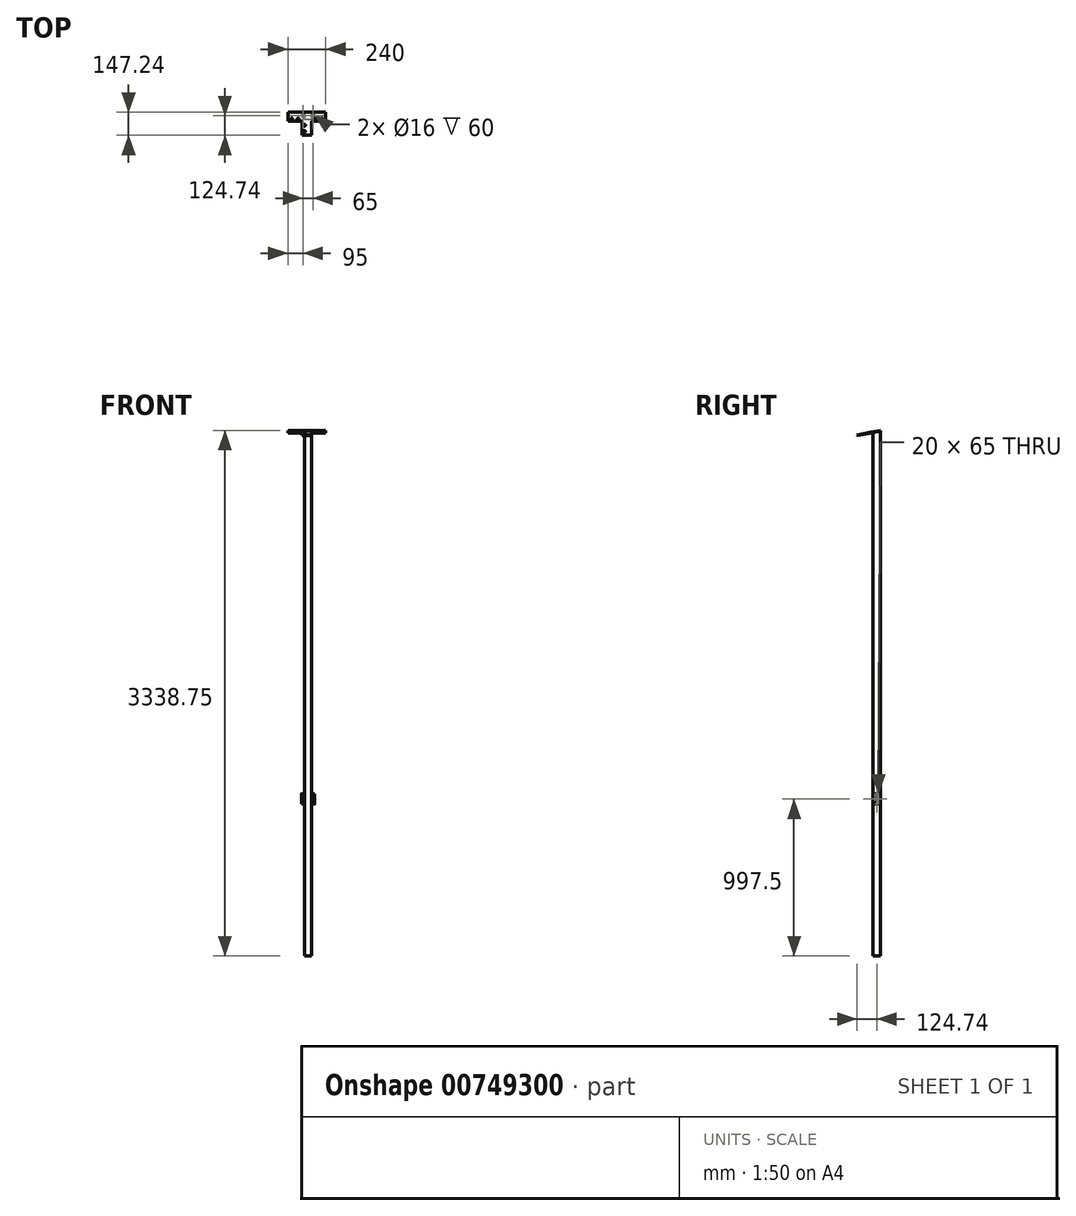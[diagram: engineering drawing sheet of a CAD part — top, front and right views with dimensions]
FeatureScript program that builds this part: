
annotation { "Feature Type Name" : "Feature", "Feature Type Description" : "" }
export const myFeature = defineFeature(function(context is Context, id is Id, definition is map)
    precondition{}
    {
        {
            var Q0;
            Q0=qCreatedBy(makeId("Top.planeOp"),FACE);
            var sketch = newSketch(context, id + "F0", { "sketchPlane" : qUnion([Q0])});
            skLineSegment(sketch, "E0.bottom", {"start": v(22.5, -22.5) * mm, "end": v(-22.5, -22.5) * mm});
            skLineSegment(sketch, "E0.top", {"start": v(22.5, 22.5) * mm, "end": v(-22.5, 22.5) * mm});
            skLineSegment(sketch, "E0.left", {"start": v(22.5, -22.5) * mm, "end": v(22.5, 22.5) * mm});
            skLineSegment(sketch, "E0.right", {"start": v(-22.5, -22.5) * mm, "end": v(-22.5, 22.5) * mm});
            skPoint(sketch, "E0.middle", {"position": v(0, 0) * mm});
            skSolve(sketch);
        }
        {
            var Q0;
            Q0=qSketchRegion(id+"F0",true);
            extrude(context, id + "F1", {"entities" : qUnion([Q0]), "depth" : 3330 * mm, "offsetDistance" : 25 * mm});
        }
        {
            var Q0;
            Q0=qCreatedBy(makeId("Top.planeOp"),FACE);
            cPlane(context, id + "F2", {"entities" : qUnion([Q0]), "cplaneType" : CPlaneType.OFFSET, "offset" : 965 * mm, "width" : 150 * mm, "height" : 150 * mm});
        }
        {
            var Q0;
            Q0=qCreatedBy(id+"F2.planeOp",FACE);
            var sketch = newSketch(context, id + "F3", { "sketchPlane" : qUnion([Q0])});
            skLineSegment(sketch, "E1", {"start": v(0, 0) * mm, "end": v(22.5, 0) * mm});
            skLineSegment(sketch, "E2", {"start": v(22.5, 0) * mm, "end": v(32.5, 0) * mm});
            skCircle(sketch, "E3", {"center": v(32.5, 0) * mm, "radius": 10 * mm});
            skLineSegment(sketch, "E4", {"start": v(32.5, 0) * mm, "end": v(32.5, 2) * mm});
            skLineSegment(sketch, "E5", {"start": v(32.5, 0) * mm, "end": v(32.5, -2) * mm});
            skLineSegment(sketch, "E6", {"start": v(32.5, -2) * mm, "end": v(22.5, -2) * mm});
            skLineSegment(sketch, "E7", {"start": v(32.5, 2) * mm, "end": v(22.5, 2) * mm});
            skLineSegment(sketch, "E8", {"start": v(0, 0) * mm, "end": v(-22.5, 0) * mm});
            skLineSegment(sketch, "E9", {"start": v(-22.5, 0) * mm, "end": v(-32.5, 0) * mm});
            skCircle(sketch, "E10", {"center": v(-32.5, 0) * mm, "radius": 10 * mm});
            skLineSegment(sketch, "E11", {"start": v(32.5, 2) * mm, "end": v(32.5, 10) * mm});
            skLineSegment(sketch, "E12", {"start": v(32.5, 10) * mm, "end": v(22.5, 10) * mm});
            skLineSegment(sketch, "E13", {"start": v(32.5, -2) * mm, "end": v(32.5, -10) * mm});
            skLineSegment(sketch, "E14", {"start": v(32.5, -10) * mm, "end": v(22.5, -10) * mm});
            skLineSegment(sketch, "E15", {"start": v(22.5, -10) * mm, "end": v(22.5, 10) * mm});
            skLineSegment(sketch, "E16", {"start": v(-32.5, 10) * mm, "end": v(-22.48, 10) * mm});
            skLineSegment(sketch, "E17", {"start": v(-22.48, 10) * mm, "end": v(-22.48, -10) * mm});
            skLineSegment(sketch, "E18", {"start": v(-22.48, -10) * mm, "end": v(-32.5, -10) * mm});
            skSolve(sketch);
        }
        {
            var Q0;
            Q0=qSketchRegion(id+"F3",true);
            extrude(context, id + "F4", {"entities" : qUnion([Q0]), "operationType" : NewBodyOperationType.ADD, "depth" : 5 * mm, "offsetDistance" : 25 * mm});
        }
        {
            var Q0;
            Q0=makeQuery(id+"F4.opExtrude","CAP_FACE",FACE,{"disambiguationData":[OSD([sQuery(id+"F3.wireOp",EDGE,"E3")])],"isStart":false});
            var sketch = newSketch(context, id + "F5", { "sketchPlane" : qUnion([Q0])});
            skCircle(sketch, "E19", {"center": v(32.5, 0) * mm, "radius": 10 * mm});
            skCircle(sketch, "E20", {"center": v(32.5, 0) * mm, "radius": 8 * mm});
            skCircle(sketch, "E21", {"center": v(-32.5, 0) * mm, "radius": 8 * mm});
            skCircle(sketch, "E22", {"center": v(-32.5, 0) * mm, "radius": 10 * mm});
            skLineSegment(sketch, "E23.0", {"start": v(32.5, -10) * mm, "end": v(22.5, -10) * mm});
            skLineSegment(sketch, "E24.0", {"start": v(22.5, -10) * mm, "end": v(22.5, 10) * mm});
            skPoint(sketch, "E25.0", {"position": v(27.5, 10) * mm});
            skLineSegment(sketch, "E26.0", {"start": v(32.5, 10) * mm, "end": v(22.5, 10) * mm});
            skLineSegment(sketch, "E27.0", {"start": v(-32.5, 10) * mm, "end": v(-22.5, 10) * mm});
            skLineSegment(sketch, "E28.0", {"start": v(-22.5, -10) * mm, "end": v(-22.5, 10) * mm});
            skLineSegment(sketch, "E29.0", {"start": v(-22.5, -10) * mm, "end": v(-32.5, -10) * mm});
            skSolve(sketch);
        }
        {
            var Q0;
            Q0=makeQuery(id+"F5.imprint","IMPRINT",FACE,{"disambiguationData":[TD([[makeQuery(id+"F5.imprint","IMPRINT",EDGE,{"derivedFrom":sQuery(id+"F5.wireOp",EDGE,"E19")}),1.0]])]});
            var Q1;
            Q1=makeQuery(id+"F5.imprint","IMPRINT",FACE,{"disambiguationData":[TD([[makeQuery(id+"F5.imprint","IMPRINT",EDGE,{"derivedFrom":sQuery(id+"F5.wireOp",EDGE,"E21")}),-1.0]])]});
            var Q2;
            {var subQ0=sQuery(id+"F5.wireOp",EDGE,"E29.0");Q2=makeQuery(id+"F5.imprint","IMPRINT",FACE,{"disambiguationData":[TD([[makeQuery(id+"F5.imprint","IMPRINT",EDGE,{"derivedFrom":subQ0}),-1.0]])]});}
            var Q3;
            {var subQ0=sQuery(id+"F5.wireOp",EDGE,"E27.0");Q3=makeQuery(id+"F5.imprint","IMPRINT",FACE,{"disambiguationData":[TD([[makeQuery(id+"F5.imprint","IMPRINT",EDGE,{"derivedFrom":subQ0}),-1.0]])]});}
            var Q4;
            {var subQ0=sQuery(id+"F5.wireOp",EDGE,"E26.0");Q4=makeQuery(id+"F5.imprint","IMPRINT",FACE,{"disambiguationData":[TD([[makeQuery(id+"F5.imprint","IMPRINT",EDGE,{"derivedFrom":subQ0}),1.0]])]});}
            var Q5;
            {var subQ0=sQuery(id+"F5.wireOp",EDGE,"E23.0");Q5=makeQuery(id+"F5.imprint","IMPRINT",FACE,{"disambiguationData":[TD([[makeQuery(id+"F5.imprint","IMPRINT",EDGE,{"derivedFrom":subQ0}),-1.0]])]});}
            extrude(context, id + "F6", {"entities" : qUnion([Q0, Q1, Q2, Q3, Q4, Q5]), "operationType" : NewBodyOperationType.ADD, "depth" : 60 * mm, "offsetDistance" : 25 * mm});
        }
        {
            var Q0;
            Q0=makeQuery(id+"F1.opExtrude","CAP_EDGE",EDGE,{"disambiguationData":[OSD([sQuery(id+"F0.wireOp",EDGE,"E0.bottom")])],"isStart":false});
            cPlane(context, id + "F7", {"entities" : qUnion([Q0]), "cplaneType" : CPlaneType.LINE_ANGLE, "offset" : 25 * mm, "angle" : 101 * degree, "oppositeDirection" : true, "width" : 150 * mm, "height" : 150 * mm});
        }
        {
            var Q0;
            Q0=makeQuery(id+"F1.opExtrude","CAP_FACE",FACE,{"disambiguationData":[OSD([sQuery(id+"F0.wireOp",EDGE,"E0.bottom"),sQuery(id+"F0.wireOp",EDGE,"E0.top"),sQuery(id+"F0.wireOp",EDGE,"E0.left"),sQuery(id+"F0.wireOp",EDGE,"E0.right")])],"isStart":false});
            var sketch = newSketch(context, id + "F8", { "sketchPlane" : qUnion([Q0])});
            skLineSegment(sketch, "E30.bottom", {"start": v(-22.5, 22.5) * mm, "end": v(22.5, 22.5) * mm});
            skLineSegment(sketch, "E30.top", {"start": v(-22.5, -22.5) * mm, "end": v(22.5, -22.5) * mm});
            skLineSegment(sketch, "E30.left", {"start": v(-22.5, 22.5) * mm, "end": v(-22.5, -22.5) * mm});
            skLineSegment(sketch, "E30.right", {"start": v(22.5, 22.5) * mm, "end": v(22.5, -22.5) * mm});
            skSolve(sketch);
        }
        {
            var Q0;
            Q0=qCreatedBy(id+"F7.planeOp",FACE);
            var sketch = newSketch(context, id + "F9", { "sketchPlane" : qUnion([Q0])});
            skLineSegment(sketch, "E31.bottom", {"start": v(-22.5, -659.15) * mm, "end": v(22.5, -659.15) * mm});
            skLineSegment(sketch, "E31.top", {"start": v(-22.5, -613.3) * mm, "end": v(22.5, -613.3) * mm});
            skLineSegment(sketch, "E31.left", {"start": v(-22.5, -659.15) * mm, "end": v(-22.5, -613.3) * mm});
            skLineSegment(sketch, "E31.right", {"start": v(22.5, -659.15) * mm, "end": v(22.5, -613.3) * mm});
            skSolve(sketch);
        }
        {
            var Q0;
            Q0=makeQuery(id+"F9.imprint","IMPRINT",FACE,{"disambiguationData":[TD([[makeQuery(id+"F9.imprint","IMPRINT",EDGE,{"derivedFrom":sQuery(id+"F9.wireOp",EDGE,"E31.bottom")}),1.0]])]});
            extrude(context, id + "F10", {"entities" : qUnion([Q0]), "operationType" : NewBodyOperationType.ADD, "depth" : 25 * mm, "offsetDistance" : 25 * mm});
        }
        {
            var Q0;
            Q0=qCreatedBy(id+"F7.planeOp",FACE);
            var sketch = newSketch(context, id + "F11", { "sketchPlane" : qUnion([Q0])});
            skLineSegment(sketch, "E32.bottom", {"start": v(-37.5, -659.15) * mm, "end": v(22.5, -659.15) * mm});
            skLineSegment(sketch, "E32.top", {"start": v(-37.5, -599.15) * mm, "end": v(22.5, -599.15) * mm});
            skLineSegment(sketch, "E32.left", {"start": v(-37.5, -659.15) * mm, "end": v(-37.5, -599.15) * mm});
            skLineSegment(sketch, "E32.right", {"start": v(22.5, -659.15) * mm, "end": v(22.5, -599.15) * mm});
            skLineSegment(sketch, "E33.bottom", {"start": v(22.5, -659.15) * mm, "end": v(112.5, -659.15) * mm});
            skLineSegment(sketch, "E33.top", {"start": v(22.5, -599.15) * mm, "end": v(112.5, -599.15) * mm});
            skLineSegment(sketch, "E33.right", {"start": v(112.5, -659.15) * mm, "end": v(112.5, -599.15) * mm});
            skLineSegment(sketch, "E34.top", {"start": v(-37.5, -509.15) * mm, "end": v(22.5, -509.15) * mm});
            skLineSegment(sketch, "E34.left", {"start": v(-37.5, -599.15) * mm, "end": v(-37.5, -509.15) * mm});
            skLineSegment(sketch, "E34.right", {"start": v(22.5, -599.15) * mm, "end": v(22.5, -509.15) * mm});
            skLineSegment(sketch, "E35", {"start": v(-37.5, -659.15) * mm, "end": v(-37.5, -509.15) * mm});
            skLineSegment(sketch, "E36", {"start": v(-37.5, -659.15) * mm, "end": v(-127.5, -659.15) * mm});
            skLineSegment(sketch, "E37", {"start": v(-127.5, -659.15) * mm, "end": v(-127.5, -599.15) * mm});
            skLineSegment(sketch, "E38", {"start": v(-127.5, -599.15) * mm, "end": v(-37.5, -599.15) * mm});
            skPoint(sketch, "E39", {"position": v(7.5, -659.15) * mm});
            skSolve(sketch);
        }
        {
            var Q0;
            Q0=qSketchRegion(id+"F11",true);
            extrude(context, id + "F12", {"entities" : qUnion([Q0]), "operationType" : NewBodyOperationType.ADD, "depth" : 5 * mm, "offsetDistance" : 25 * mm});
        }
        {
            var Q0;
            Q0=makeQuery(id+"F12.boolean.opBoolean","MERGE",FACE,{"derivedFrom":[makeQuery(id+"F10.opExtrude","CAP_FACE",FACE,{"disambiguationData":[OSD([sQuery(id+"F9.wireOp",EDGE,"E31.bottom"),sQuery(id+"F9.wireOp",EDGE,"E31.top"),sQuery(id+"F9.wireOp",EDGE,"E31.left"),sQuery(id+"F9.wireOp",EDGE,"E31.right")])],"isStart":true}),makeQuery(id+"F12.opExtrude","CAP_FACE",FACE,{"disambiguationData":[OSD([sQuery(id+"F11.wireOp",EDGE,"E32.bottom"),sQuery(id+"F11.wireOp",EDGE,"E33.bottom"),sQuery(id+"F11.wireOp",EDGE,"E33.top"),sQuery(id+"F11.wireOp",EDGE,"E33.right"),sQuery(id+"F11.wireOp",EDGE,"E34.top"),sQuery(id+"F11.wireOp",EDGE,"E34.right"),sQuery(id+"F11.wireOp",EDGE,"E35")])],"isStart":true})]});
            var sketch = newSketch(context, id + "F13", { "sketchPlane" : qUnion([Q0])});
            skLineSegment(sketch, "E40", {"start": v(22.5, 509.15) * mm, "end": v(22.5, 534.15) * mm});
            skLineSegment(sketch, "E41", {"start": v(-22.5, 534.15) * mm, "end": v(-22.5, 574.15) * mm});
            skLineSegment(sketch, "E42", {"start": v(112.5, 599.15) * mm, "end": v(87.5, 599.15) * mm});
            skLineSegment(sketch, "E43", {"start": v(87.5, 599.15) * mm, "end": v(87.5, 614.15) * mm});
            skLineSegment(sketch, "E44", {"start": v(87.5, 614.15) * mm, "end": v(47.5, 614.15) * mm});
            skCircle(sketch, "E45", {"center": v(87.5, 614.15) * mm, "radius": 6 * mm});
            skCircle(sketch, "E46", {"center": v(47.5, 614.15) * mm, "radius": 6 * mm});
            skLineSegment(sketch, "E47", {"start": v(-22.5, 509.15) * mm, "end": v(-22.5, 602.33) * mm});
            skCircle(sketch, "E48.MirrorC", {"center": v(-22.5, 574.15) * mm, "radius": 6 * mm});
            skCircle(sketch, "E49.MirrorC", {"center": v(-22.5, 534.15) * mm, "radius": 6 * mm});
            skCircle(sketch, "E50.MirrorC", {"center": v(-62.5, 614.15) * mm, "radius": 6 * mm});
            skCircle(sketch, "E51.MirrorC", {"center": v(-102.5, 614.15) * mm, "radius": 6 * mm});
            skLineSegment(sketch, "E52", {"start": v(-22.5, 534.15) * mm, "end": v(-37.5, 534.15) * mm});
            skSolve(sketch);
        }
        {
            var Q0;
            Q0=qSketchRegion(id+"F13",true);
            extrude(context, id + "F14", {"entities" : qUnion([Q0]), "operationType" : NewBodyOperationType.REMOVE, "oppositeDirection" : true, "depth" : 25 * mm, "offsetDistance" : 25 * mm});
        }
        {
            var Q0;
            Q0=qCreatedBy(makeId("Top.planeOp"),FACE);
            var sketch = newSketch(context, id + "F15", { "sketchPlane" : qUnion([Q0])});
            skLineSegment(sketch, "E53.bottom", {"start": v(-22.5, 22.5) * mm, "end": v(127.5, 22.5) * mm});
            skLineSegment(sketch, "E53.top", {"start": v(-22.5, 27.27) * mm, "end": v(127.5, 27.27) * mm});
            skLineSegment(sketch, "E53.left", {"start": v(-22.5, 22.5) * mm, "end": v(-22.5, 27.27) * mm});
            skLineSegment(sketch, "E53.right", {"start": v(127.5, 22.5) * mm, "end": v(127.5, 27.27) * mm});
            skSolve(sketch);
        }
        {
            var Q0;
            Q0=qSketchRegion(id+"F15",true);
            extrude(context, id + "F16", {"entities" : qUnion([Q0]), "operationType" : NewBodyOperationType.REMOVE, "depth" : 3358.7 * mm, "offsetDistance" : 25 * mm});
        }
        {
            var Q0;
            Q0=makeQuery(id+"F16.boolean.opBoolean","COPY",FACE,{"derivedFrom":makeQuery(id+"F16.opExtrude","SWEPT_FACE",FACE,{"disambiguationData":[OSD([sQuery(id+"F15.wireOp",EDGE,"E53.left")])]})});
            var sketch = newSketch(context, id + "F17", { "sketchPlane" : qUnion([Q0])});
            skLineSegment(sketch, "E54", {"start": v(22.5, 3333.65) * mm, "end": v(23.45, 3333.84) * mm});
            skLineSegment(sketch, "E55", {"start": v(23.45, 3333.84) * mm, "end": v(22.5, 3338.75) * mm});
            skLineSegment(sketch, "E56", {"start": v(22.5, 3338.75) * mm, "end": v(22.5, 3333.65) * mm});
            skSolve(sketch);
        }
        {
            var Q0;
            Q0 = qSketchRegion(id + "F17", true);
            extrude(context, id + "F18", {"entities" : qUnion([Q0]), "operationType" : NewBodyOperationType.REMOVE, "oppositeDirection" : true, "depth" : 106.2 * mm, "offsetDistance" : 25 * mm});
        }
    });
